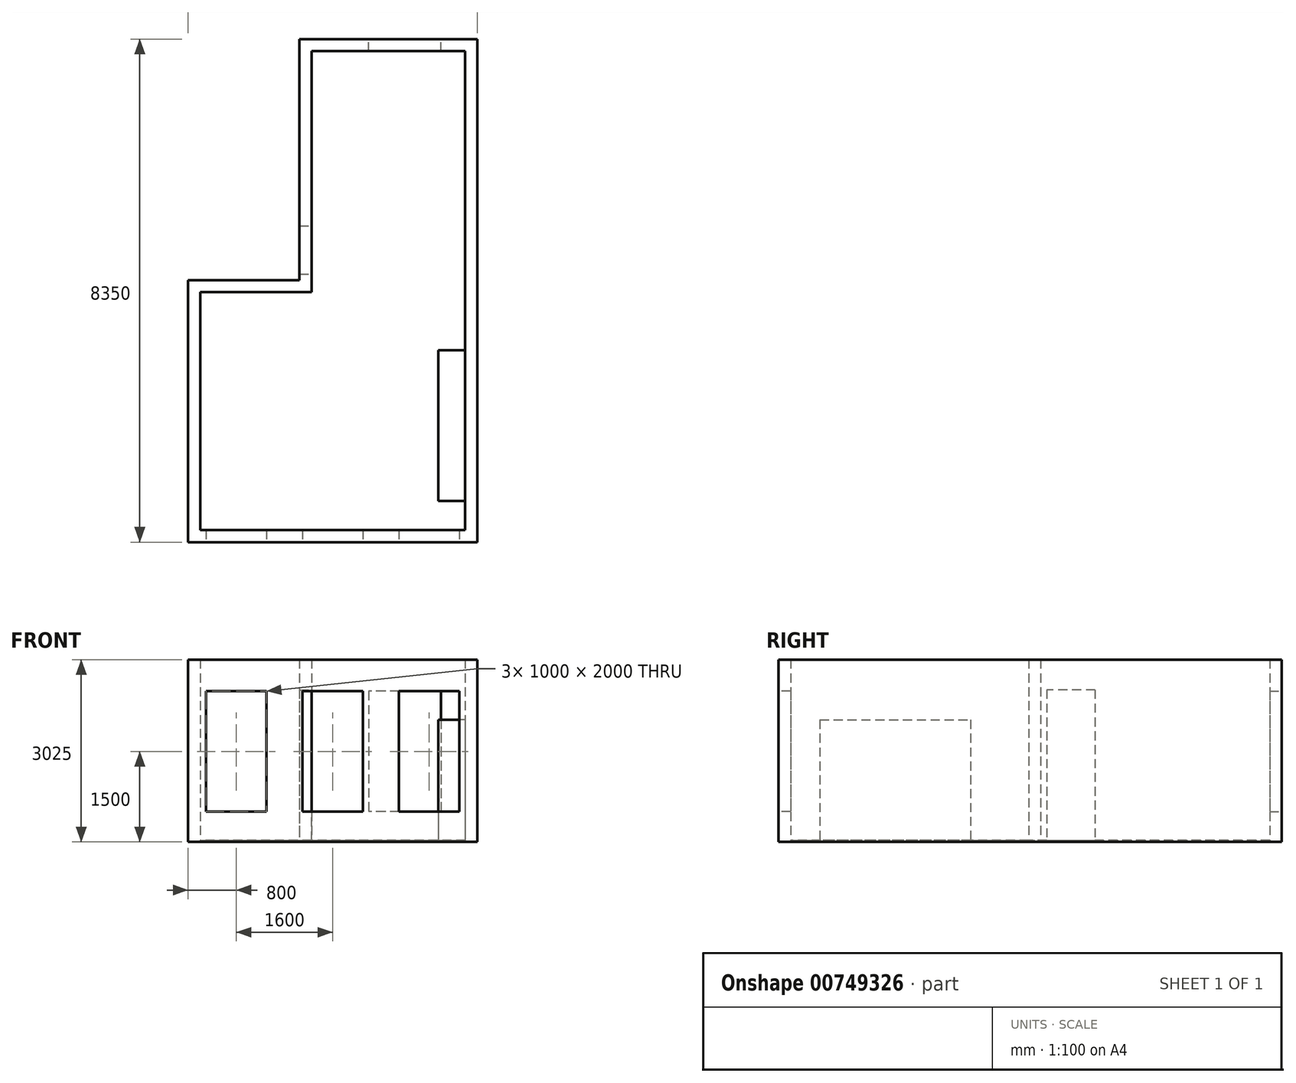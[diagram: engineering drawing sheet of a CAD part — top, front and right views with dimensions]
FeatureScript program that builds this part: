
annotation { "Feature Type Name" : "Feature", "Feature Type Description" : "" }
export const myFeature = defineFeature(function(context is Context, id is Id, definition is map)
    precondition{}
    {
        {
            var Q0;
            Q0=qCreatedBy(makeId("Top.planeOp"),FACE);
            var sketch = newSketch(context, id + "F0", { "sketchPlane" : qUnion([Q0])});
            skLineSegment(sketch, "E0", {"start": v(0, 0) * mm, "end": v(4800, 0) * mm});
            skLineSegment(sketch, "E1", {"start": v(4800, 0) * mm, "end": v(4800, 8350) * mm});
            skLineSegment(sketch, "E2", {"start": v(4800, 8350) * mm, "end": v(1850, 8350) * mm});
            skLineSegment(sketch, "E3", {"start": v(1850, 8350) * mm, "end": v(1850, 4350) * mm});
            skLineSegment(sketch, "E4", {"start": v(1850, 4350) * mm, "end": v(0, 4350) * mm});
            skLineSegment(sketch, "E5", {"start": v(0, 4350) * mm, "end": v(0, 0) * mm});
            skSolve(sketch);
        }
        {
            var Q0;
            Q0 = qSketchRegion(id + "F0", true);
            extrude(context, id + "F1", {"entities" : qUnion([Q0]), "depth" : 25 * mm, "offsetDistance" : 25 * mm});
        }
        {
            var Q0;
            Q0=qCreatedBy(makeId("Top.planeOp"),FACE);
            var sketch = newSketch(context, id + "F2", { "sketchPlane" : qUnion([Q0])});
            skSolve(sketch);
        }
        {
            var Q0;
            Q0=makeQuery(id+"F1.opExtrude","CAP_FACE",FACE,{"disambiguationData":[OSD([sQuery(id+"F0.wireOp",EDGE,"E0"),sQuery(id+"F0.wireOp",EDGE,"E1"),sQuery(id+"F0.wireOp",EDGE,"E2"),sQuery(id+"F0.wireOp",EDGE,"E3"),sQuery(id+"F0.wireOp",EDGE,"E4"),sQuery(id+"F0.wireOp",EDGE,"E5")])],"isStart":false});
            var sketch = newSketch(context, id + "F3", { "sketchPlane" : qUnion([Q0])});
            skLineSegment(sketch, "E6.0", {"start": v(4600, 200) * mm, "end": v(4600, 8150) * mm});
            skLineSegment(sketch, "E6.1", {"start": v(2050, 8150) * mm, "end": v(2050, 4150) * mm});
            skLineSegment(sketch, "E6.2", {"start": v(2050, 4150) * mm, "end": v(200, 4150) * mm});
            skLineSegment(sketch, "E6.3", {"start": v(4600, 8150) * mm, "end": v(2050, 8150) * mm});
            skLineSegment(sketch, "E6.4", {"start": v(200, 4150) * mm, "end": v(200, 200) * mm});
            skLineSegment(sketch, "E6.5", {"start": v(200, 200) * mm, "end": v(4600, 200) * mm});
            skLineSegment(sketch, "E7.0", {"start": v(4800, 0) * mm, "end": v(4800, 8350) * mm});
            skLineSegment(sketch, "E7.1", {"start": v(1850, 8350) * mm, "end": v(1850, 4350) * mm});
            skLineSegment(sketch, "E7.2", {"start": v(1850, 4350) * mm, "end": v(0, 4350) * mm});
            skLineSegment(sketch, "E7.3", {"start": v(4800, 8350) * mm, "end": v(1850, 8350) * mm});
            skLineSegment(sketch, "E7.4", {"start": v(0, 4350) * mm, "end": v(0, 0) * mm});
            skLineSegment(sketch, "E7.5", {"start": v(0, 0) * mm, "end": v(4800, 0) * mm});
            skSolve(sketch);
        }
        {
            var Q0;
            Q0 = qSketchRegion(id + "F3", true);
            extrude(context, id + "F4", {"entities" : qUnion([Q0]), "operationType" : NewBodyOperationType.ADD, "depth" : 3000 * mm, "offsetDistance" : 25 * mm});
        }
        {
            var Q0;
            Q0=makeQuery(id+"F4.boolean.opBoolean","MERGE",FACE,{"derivedFrom":[makeQuery(id+"F1.opExtrude","SWEPT_FACE",FACE,{"disambiguationData":[OSD([sQuery(id+"F0.wireOp",EDGE,"E0")])]}),makeQuery(id+"F4.opExtrude","SWEPT_FACE",FACE,{"disambiguationData":[OSD([sQuery(id+"F3.wireOp",EDGE,"E7.5")])]})]});
            var sketch = newSketch(context, id + "F5", { "sketchPlane" : qUnion([Q0])});
            skLineSegment(sketch, "E8.bottom", {"start": v(300, 2500) * mm, "end": v(1300, 2500) * mm});
            skLineSegment(sketch, "E8.top", {"start": v(300, 500) * mm, "end": v(1300, 500) * mm});
            skLineSegment(sketch, "E8.left", {"start": v(300, 2500) * mm, "end": v(300, 500) * mm});
            skLineSegment(sketch, "E8.right", {"start": v(1300, 2500) * mm, "end": v(1300, 500) * mm});
            skLineSegment(sketch, "E9.bottom", {"start": v(1900, 2500) * mm, "end": v(2900, 2500) * mm});
            skLineSegment(sketch, "E9.top", {"start": v(1900, 500) * mm, "end": v(2900, 500) * mm});
            skLineSegment(sketch, "E9.left", {"start": v(1900, 2500) * mm, "end": v(1900, 500) * mm});
            skLineSegment(sketch, "E9.right", {"start": v(2900, 2500) * mm, "end": v(2900, 500) * mm});
            skLineSegment(sketch, "E10.bottom", {"start": v(3500, 2500) * mm, "end": v(4500, 2500) * mm});
            skLineSegment(sketch, "E10.top", {"start": v(3500, 500) * mm, "end": v(4500, 500) * mm});
            skLineSegment(sketch, "E10.left", {"start": v(3500, 2500) * mm, "end": v(3500, 500) * mm});
            skLineSegment(sketch, "E10.right", {"start": v(4500, 2500) * mm, "end": v(4500, 500) * mm});
            skLineSegment(sketch, "E11", {"start": v(300, 2500) * mm, "end": v(0, 2500) * mm, "construction": true});
            skLineSegment(sketch, "E12", {"start": v(4500, 2500) * mm, "end": v(4800, 2500) * mm, "construction": true});
            skSolve(sketch);
        }
        {
            var Q0;
            Q0 = qSketchRegion(id + "F5", true);
            extrude(context, id + "F6", {"entities" : qUnion([Q0]), "operationType" : NewBodyOperationType.REMOVE, "endBound" : BoundingType.UP_TO_NEXT, "oppositeDirection" : true, "depth" : 25 * mm, "offsetDistance" : 25 * mm});
        }
        {
            var Q0;
            Q0=makeQuery(id+"F4.boolean.opBoolean","MERGE",FACE,{"derivedFrom":[makeQuery(id+"F1.opExtrude","SWEPT_FACE",FACE,{"disambiguationData":[OSD([sQuery(id+"F0.wireOp",EDGE,"E2")])]}),makeQuery(id+"F4.opExtrude","SWEPT_FACE",FACE,{"disambiguationData":[OSD([sQuery(id+"F3.wireOp",EDGE,"E7.3")])]})]});
            var sketch = newSketch(context, id + "F7", { "sketchPlane" : qUnion([Q0])});
            skLineSegment(sketch, "E13.bottom", {"start": v(-4200, 2500) * mm, "end": v(-3000, 2500) * mm});
            skLineSegment(sketch, "E13.top", {"start": v(-4200, 500) * mm, "end": v(-3000, 500) * mm});
            skLineSegment(sketch, "E13.left", {"start": v(-4200, 2500) * mm, "end": v(-4200, 500) * mm});
            skLineSegment(sketch, "E13.right", {"start": v(-3000, 2500) * mm, "end": v(-3000, 500) * mm});
            skLineSegment(sketch, "E14", {"start": v(-4200, 2500) * mm, "end": v(-4800, 2500) * mm, "construction": true});
            skSolve(sketch);
        }
        {
            var Q0;
            Q0 = qSketchRegion(id + "F7", true);
            extrude(context, id + "F8", {"entities" : qUnion([Q0]), "operationType" : NewBodyOperationType.REMOVE, "endBound" : BoundingType.UP_TO_NEXT, "oppositeDirection" : true, "depth" : 25 * mm, "offsetDistance" : 25 * mm});
        }
        {
            var Q0;
            Q0=makeQuery(id+"F4.opExtrude","SWEPT_FACE",FACE,{"disambiguationData":[OSD([sQuery(id+"F3.wireOp",EDGE,"E6.1")])]});
            var sketch = newSketch(context, id + "F9", { "sketchPlane" : qUnion([Q0])});
            skLineSegment(sketch, "E15.bottom", {"start": v(4450, 25) * mm, "end": v(5250, 25) * mm});
            skLineSegment(sketch, "E15.top", {"start": v(4450, 2525) * mm, "end": v(5250, 2525) * mm});
            skLineSegment(sketch, "E15.left", {"start": v(4450, 25) * mm, "end": v(4450, 2525) * mm});
            skLineSegment(sketch, "E15.right", {"start": v(5250, 25) * mm, "end": v(5250, 2525) * mm});
            skSolve(sketch);
        }
        {
            var Q0;
            Q0 = qSketchRegion(id + "F9", true);
            extrude(context, id + "F10", {"entities" : qUnion([Q0]), "operationType" : NewBodyOperationType.REMOVE, "endBound" : BoundingType.UP_TO_NEXT, "oppositeDirection" : true, "depth" : 25 * mm, "offsetDistance" : 25 * mm});
        }
        {
            var Q0;
            Q0=makeQuery(id+"F10.boolean.opBoolean","MERGE",FACE,{"derivedFrom":[makeQuery(id+"F1.opExtrude","CAP_FACE",FACE,{"disambiguationData":[OSD([sQuery(id+"F0.wireOp",EDGE,"E0"),sQuery(id+"F0.wireOp",EDGE,"E1"),sQuery(id+"F0.wireOp",EDGE,"E2"),sQuery(id+"F0.wireOp",EDGE,"E3"),sQuery(id+"F0.wireOp",EDGE,"E4"),sQuery(id+"F0.wireOp",EDGE,"E5")])],"isStart":false}),makeQuery(id+"F10.opExtrude","SWEPT_FACE",FACE,{"disambiguationData":[OSD([sQuery(id+"F9.wireOp",EDGE,"E15.bottom")])]})]});
            var sketch = newSketch(context, id + "F11", { "sketchPlane" : qUnion([Q0])});
            skLineSegment(sketch, "E16.bottom", {"start": v(4600, 3183.84) * mm, "end": v(4150, 3183.84) * mm});
            skLineSegment(sketch, "E16.top", {"start": v(4600, 683.84) * mm, "end": v(4150, 683.84) * mm});
            skLineSegment(sketch, "E16.left", {"start": v(4600, 3183.84) * mm, "end": v(4600, 683.84) * mm});
            skLineSegment(sketch, "E16.right", {"start": v(4150, 3183.84) * mm, "end": v(4150, 683.84) * mm});
            skSolve(sketch);
        }
        {
            var Q0;
            Q0 = qSketchRegion(id + "F11", true);
            extrude(context, id + "F12", {"entities" : qUnion([Q0]), "operationType" : NewBodyOperationType.ADD, "depth" : 2000 * mm, "offsetDistance" : 25 * mm});
        }
    });
